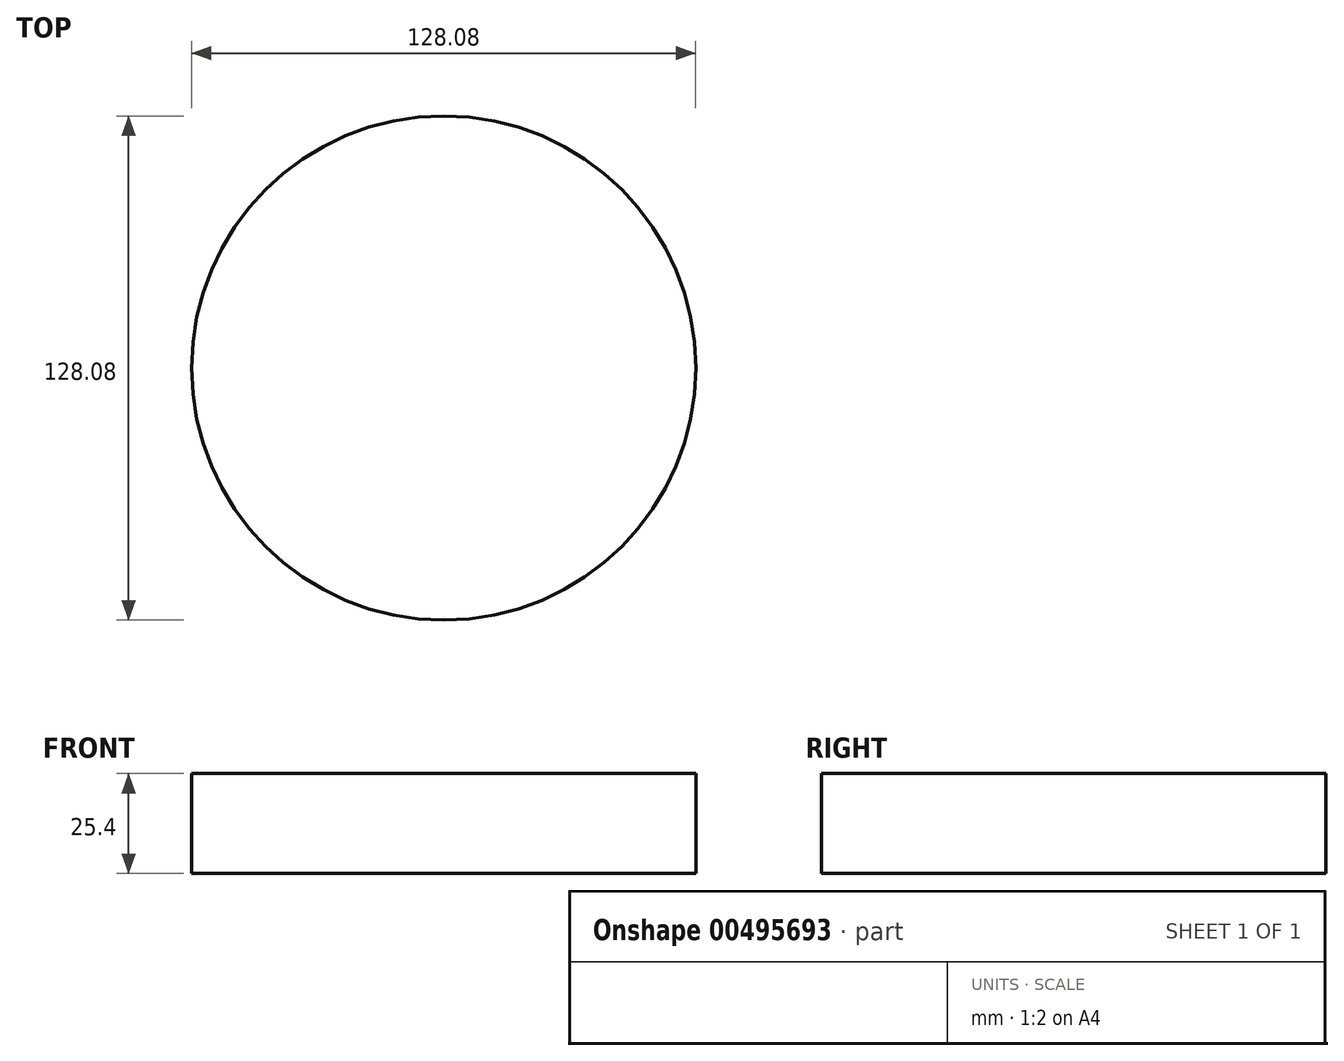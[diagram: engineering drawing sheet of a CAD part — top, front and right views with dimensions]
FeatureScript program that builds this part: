
annotation { "Feature Type Name" : "Feature", "Feature Type Description" : "" }
export const myFeature = defineFeature(function(context is Context, id is Id, definition is map)
    precondition{}
    {
        {
            var Q0;
            Q0=qCreatedBy(makeId("Top.planeOp"),FACE);
            var sketch = newSketch(context, id + "F0", { "sketchPlane" : qUnion([Q0])});
            skCircle(sketch, "E0", {"center": v(0, 0) * mm, "radius": 64.04 * mm});
            skSolve(sketch);
        }
        {
            var Q0;
            Q0=makeQuery(id+"F0.imprint","IMPRINT",FACE,{"disambiguationData":[TD([[makeQuery(id+"F0.imprint","IMPRINT",EDGE,{"derivedFrom":sQuery(id+"F0.wireOp",EDGE,"E0")}),1.0]])]});
            extrude(context, id + "F1", {"entities" : qUnion([Q0]), "depth" : 25.4 * mm});
        }
    });
